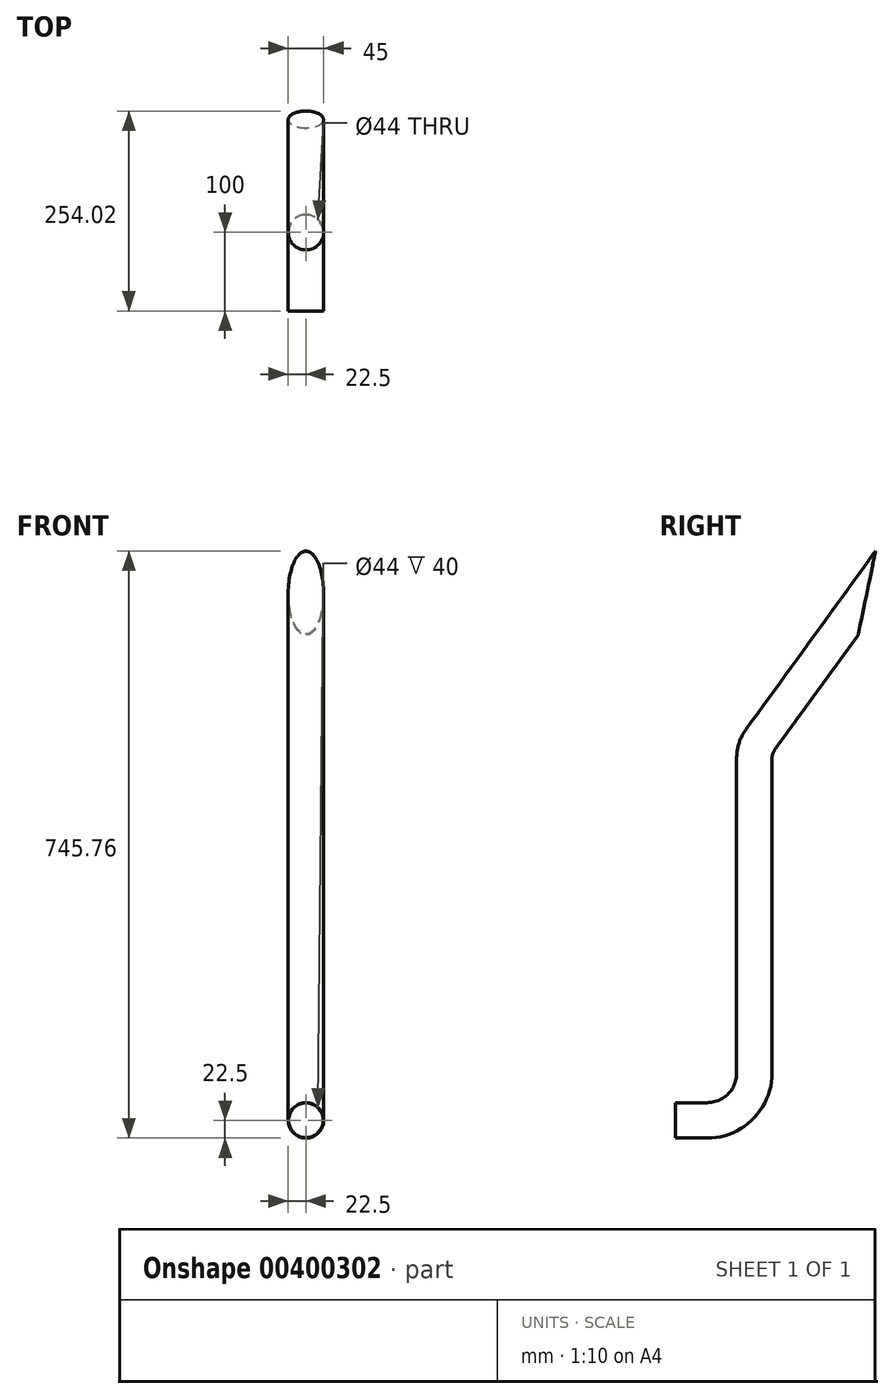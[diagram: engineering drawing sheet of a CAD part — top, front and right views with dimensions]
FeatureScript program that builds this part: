
annotation { "Feature Type Name" : "Feature", "Feature Type Description" : "" }
export const myFeature = defineFeature(function(context is Context, id is Id, definition is map)
    precondition{}
    {
        {
            var Q0;
            Q0=qCreatedBy(makeId("Right.planeOp"),FACE);
            var sketch = newSketch(context, id + "F0", { "sketchPlane" : qUnion([Q0])});
            skLineSegment(sketch, "E0", {"start": v(0, 0) * mm, "end": v(40, 0) * mm});
            skLineSegment(sketch, "E1", {"start": v(100, 60) * mm, "end": v(100, 460) * mm});
            skLineSegment(sketch, "E2", {"start": v(107.64, 483.51) * mm, "end": v(272.22, 710.04) * mm});
            skPoint(sketch, "E3.visualSharp", {"position": v(100, 0) * mm});
            skArc(sketch, "E3.filletArc", {"start": v(40, 0) * mm, "mid": v(82.43, 17.57) * mm, "end": v(100, 60) * mm});
            skPoint(sketch, "E4.visualSharp", {"position": v(100, 473) * mm});
            skArc(sketch, "E4.filletArc", {"start": v(107.64, 483.51) * mm, "mid": v(101.96, 472.36) * mm, "end": v(100, 460) * mm});
            skPoint(sketch, "E5.visualSharp", {"position": v(175.47, 576.87) * mm});
            skSolve(sketch);
        }
        {
            var Q0;
            Q0=qCreatedBy(makeId("Front.planeOp"),FACE);
            var sketch = newSketch(context, id + "F1", { "sketchPlane" : qUnion([Q0])});
            skCircle(sketch, "E6", {"center": v(0, 0) * mm, "radius": 22 * mm});
            skCircle(sketch, "E7", {"center": v(0, 0) * mm, "radius": 22.5 * mm});
            skSolve(sketch);
        }
        {
            var Q0;
            Q0=makeQuery(id+"F1.imprint","IMPRINT",FACE,{"disambiguationData":[TD([[makeQuery(id+"F1.imprint","IMPRINT",EDGE,{"derivedFrom":sQuery(id+"F1.wireOp",EDGE,"E6")}),-1.0]])]});
            var Q1;
            Q1=sQuery(id+"F0.wireOp",EDGE,"E0");
            var Q2;
            Q2=sQuery(id+"F0.wireOp",EDGE,"E3.filletArc");
            var Q3;
            Q3=sQuery(id+"F0.wireOp",EDGE,"E1");
            var Q4;
            Q4=sQuery(id+"F0.wireOp",EDGE,"E4.filletArc");
            var Q5;
            Q5=sQuery(id+"F0.wireOp",EDGE,"E2");
            var Q6;
            Q6=sQuery(id+"F0.wireOp",EDGE,"E5.filletArc");
            var Q7;
            Q7=sQuery(id+"F0.wireOp",EDGE,"ADRPB93s-L3ns-Njq6-n3NY-gjiRkliPrde4");
            sweep(context, id + "F2", {"profiles" : qUnion([Q0]), "path" : qUnion([Q1, Q2, Q3, Q4, Q5, Q6, Q7])});
        }
        {
            var Q0;
            Q0=qCreatedBy(makeId("Right.planeOp"),FACE);
            var sketch = newSketch(context, id + "F3", { "sketchPlane" : qUnion([Q0])});
            skLineSegment(sketch, "E8", {"start": v(145.31, 573.64) * mm, "end": v(254.02, 723.26) * mm});
            skLineSegment(sketch, "E9", {"start": v(290.42, 696.81) * mm, "end": v(173.02, 535.22) * mm});
            skLineSegment(sketch, "E10", {"start": v(254.02, 723.26) * mm, "end": v(231.72, 616.02) * mm});
            skLineSegment(sketch, "E11", {"start": v(231.72, 616.02) * mm, "end": v(290.42, 696.81) * mm});
            skLineSegment(sketch, "E12", {"start": v(254.02, 723.26) * mm, "end": v(290.42, 696.81) * mm});
            skSolve(sketch);
        }
        {
            var Q0;
            Q0 = qSketchRegion(id + "F3", true);
            extrude(context, id + "F4", {"entities" : qUnion([Q0]), "operationType" : NewBodyOperationType.REMOVE, "endBound" : BoundingType.THROUGH_ALL, "depth" : 25 * mm});
        }
        {
            var Q0;
            Q0 = qSketchRegion(id + "F3", true);
            extrude(context, id + "F5", {"entities" : qUnion([Q0]), "operationType" : NewBodyOperationType.REMOVE, "oppositeDirection" : true, "depth" : 25 * mm});
        }
    });
